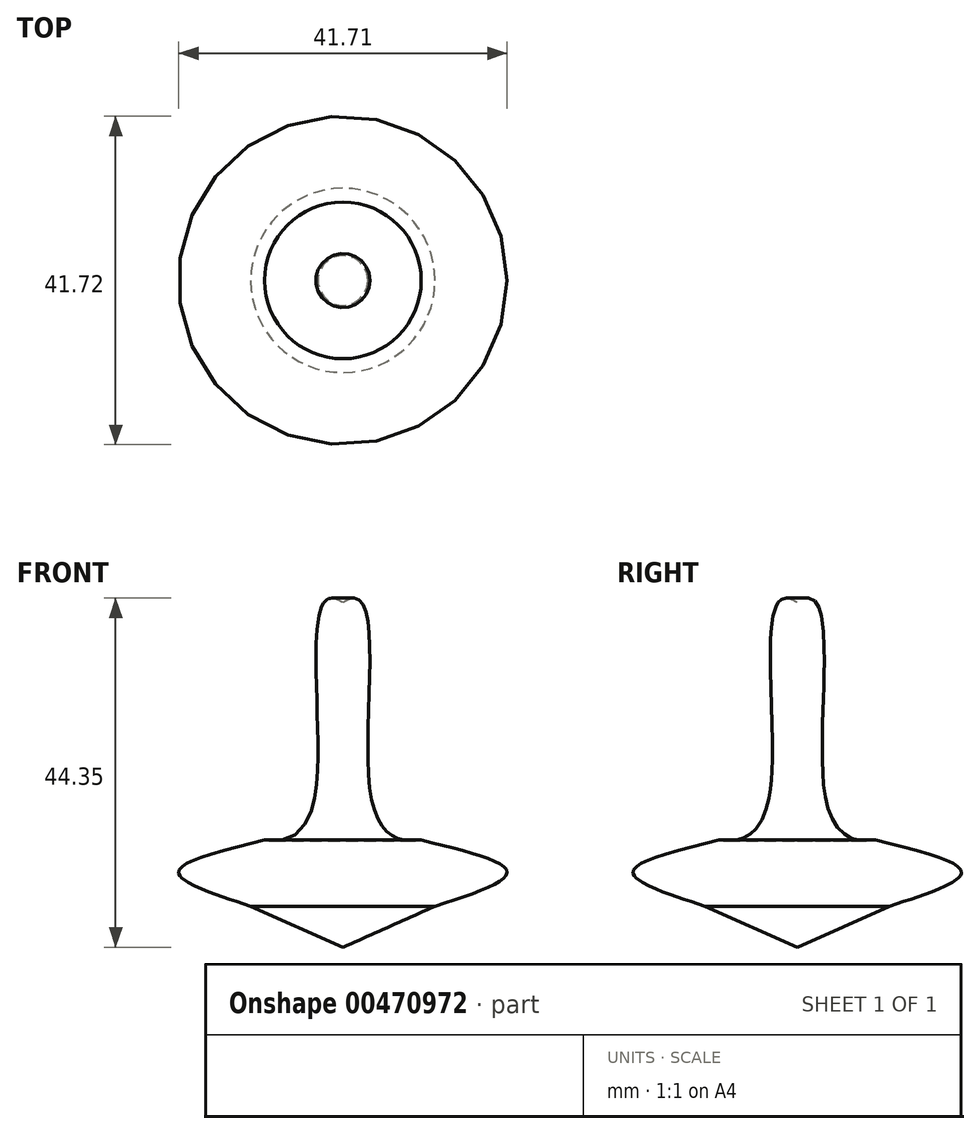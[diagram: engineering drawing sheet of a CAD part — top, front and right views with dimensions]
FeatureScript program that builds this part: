
annotation { "Feature Type Name" : "Feature", "Feature Type Description" : "" }
export const myFeature = defineFeature(function(context is Context, id is Id, definition is map)
    precondition{}
    {
        {
            var Q0;
            Q0=qCreatedBy(makeId("Front.planeOp"),FACE);
            var sketch = newSketch(context, id + "F0", { "sketchPlane" : qUnion([Q0])});
            skLineSegment(sketch, "E0", {"start": v(0, 0) * mm, "end": v(0, 43.79) * mm});
            skFitSpline(sketch, "E1", {"points": [v(0, 43.79) * mm, v(3.5, 19.5) * mm, v(9.95, 13.61) * mm], "startDerivative": vector(28.02, 19.97) * mm, "endDerivative": vector(23.9, 3.94) * mm});
            skLineSegment(sketch, "E2", {"start": v(0, 0) * mm, "end": v(11.7, 5.22) * mm});
            skFitSpline(sketch, "E3", {"points": [v(11.7, 5.22) * mm, v(20.86, 9.53) * mm, v(9.95, 13.61) * mm], "startDerivative": vector(28.67, 9.21) * mm, "endDerivative": vector(-31.51, 7.6) * mm});
            skPoint(sketch, "E4.endSnap0", {"position": v(5.85, 2.6) * mm});
            skLineSegment(sketch, "E5.MirrorCS", {"start": v(0, 87.57) * mm, "end": v(0, 43.79) * mm});
            skSolve(sketch);
        }
        {
            var Q0;
            Q0=sQuery(id+"F0.wireOp",EDGE,"E2");
            var Q1;
            Q1=sQuery(id+"F0.wireOp",EDGE,"E1");
            var Q2;
            Q2=sQuery(id+"F0.wireOp",EDGE,"E3");
            var Q3;
            Q3=sQuery(id+"F0.wireOp",EDGE,"E0");
            revolve(context, id + "F1", {"bodyType" : ToolBodyType.SURFACE, "surfaceEntities" : qUnion([Q0, Q1, Q2]), "axis" : qUnion([Q3]), "revolveType" : RevolveType.FULL});
        }
    });
